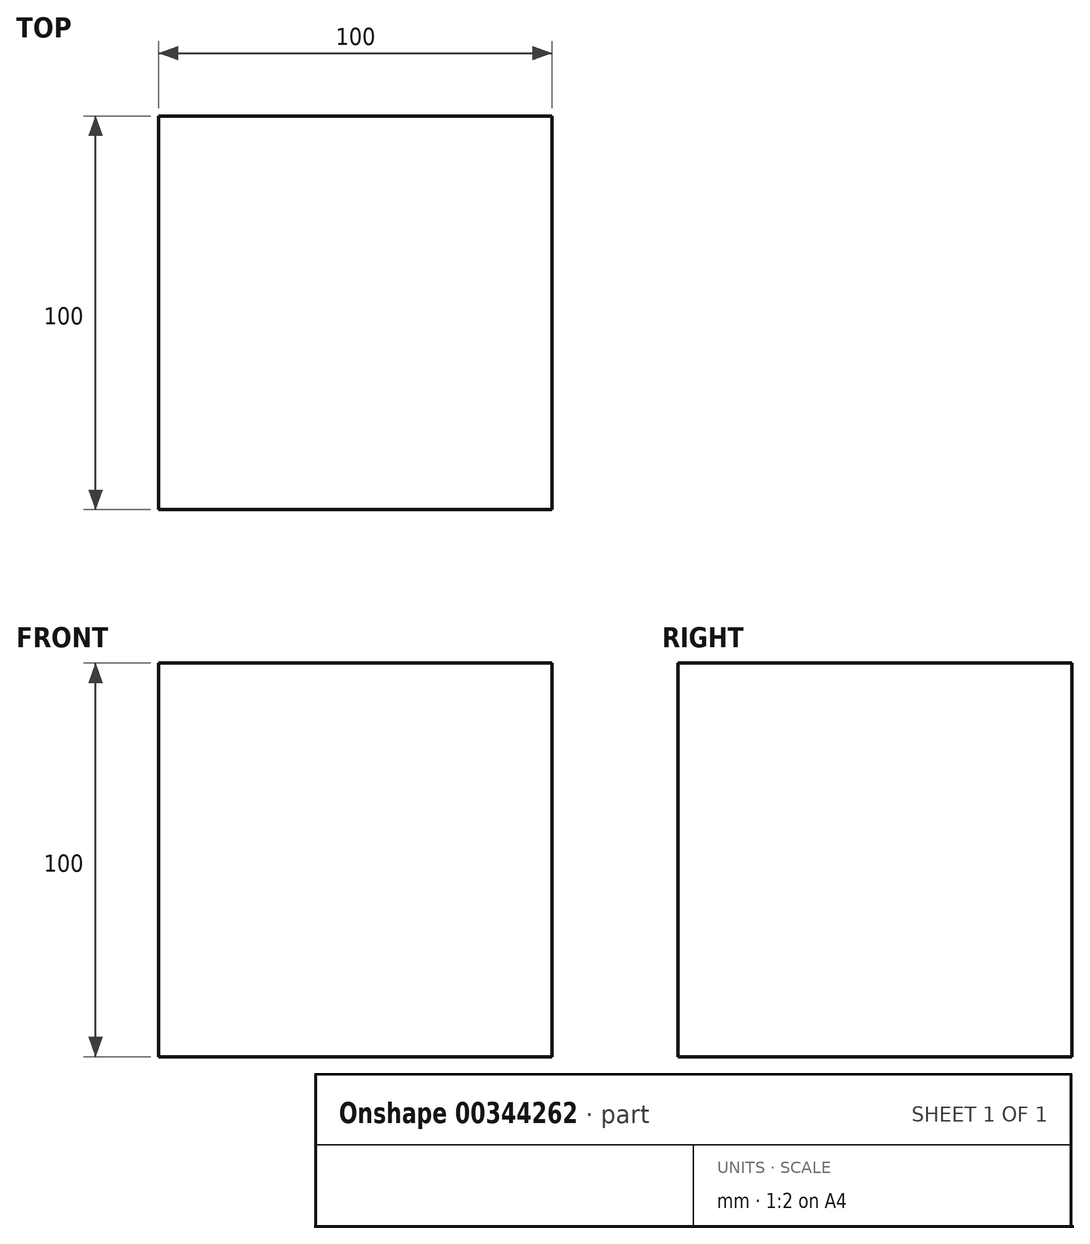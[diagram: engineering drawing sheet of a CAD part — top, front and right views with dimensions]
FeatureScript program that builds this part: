
annotation { "Feature Type Name" : "Feature", "Feature Type Description" : "" }
export const myFeature = defineFeature(function(context is Context, id is Id, definition is map)
    precondition{}
    {
        {
            var Q0;
            Q0=qCreatedBy(makeId("Top.planeOp"),FACE);
            var sketch = newSketch(context, id + "F0", { "sketchPlane" : qUnion([Q0])});
            skLineSegment(sketch, "E0.bottom", {"start": v(50, -50) * mm, "end": v(-50, -50) * mm});
            skLineSegment(sketch, "E0.top", {"start": v(50, 50) * mm, "end": v(-50, 50) * mm});
            skLineSegment(sketch, "E0.left", {"start": v(50, -50) * mm, "end": v(50, 50) * mm});
            skLineSegment(sketch, "E0.right", {"start": v(-50, -50) * mm, "end": v(-50, 50) * mm});
            skPoint(sketch, "E0.middle", {"position": v(0, 0) * mm});
            skSolve(sketch);
        }
        {
            var Q0;
            Q0=makeQuery(id+"F0.imprint","IMPRINT",FACE,{"disambiguationData":[TD([[makeQuery(id+"F0.imprint","IMPRINT",EDGE,{"derivedFrom":sQuery(id+"F0.wireOp",EDGE,"E0.bottom")}),-1.0]])]});
            extrude(context, id + "F1", {"entities" : qUnion([Q0]), "depth" : 100 * mm});
        }
    });
